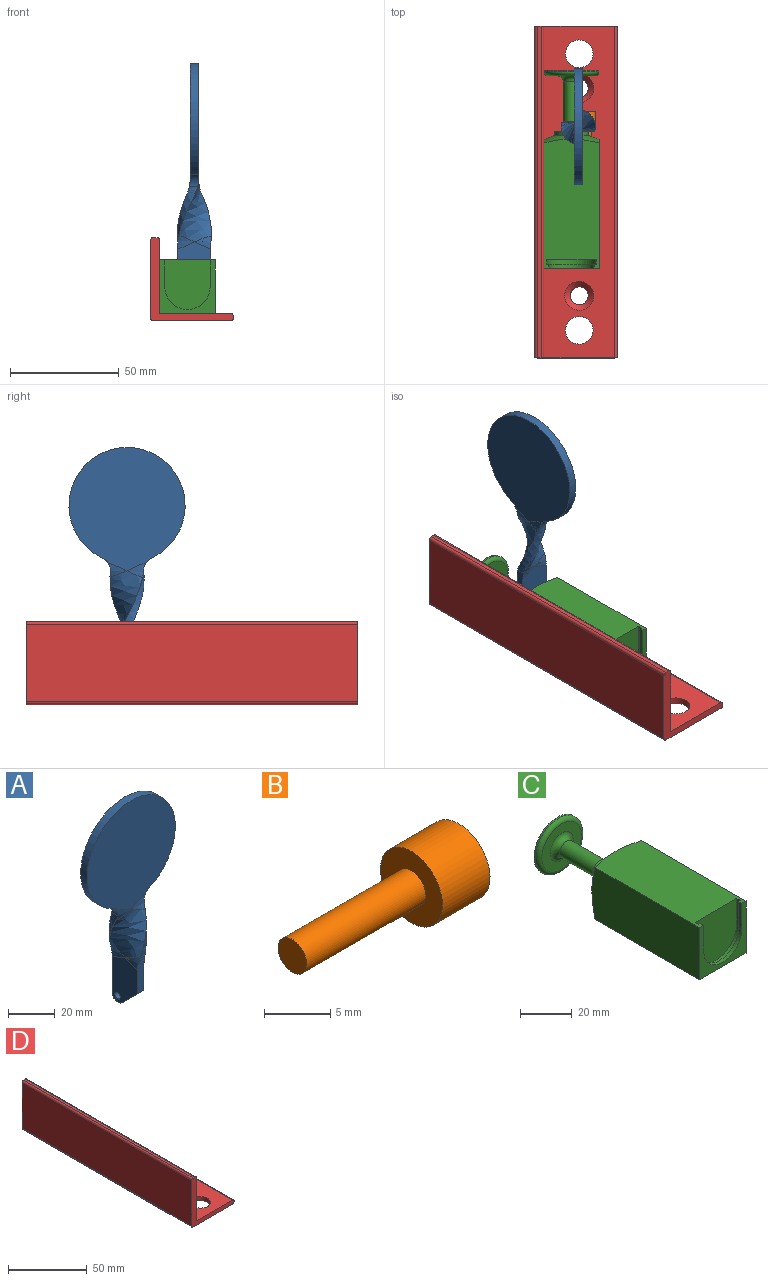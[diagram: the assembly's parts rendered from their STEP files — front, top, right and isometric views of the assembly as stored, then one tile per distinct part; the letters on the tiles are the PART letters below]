
ASSEMBLY  parts=4 mates=6
PART A: 26 faces, bbox 55x24.1x109.1 mm
  f0: plane 56.59x53.34mm, normal (0,-1,0), area 2267.7mm2, adj f2,f3,f4,f20,f21
  f1: plane 58.14x54.89mm, normal (0,1,0), area 2267.7mm2, adj f2,f3,f4,f18,f19
  f2: cylinder r=6.35mm len=5.75mm, axis (0,1,0), area 27.5mm2, adj f0,f1,f4,f5,f18,f20
  f3: cylinder r=6.35mm len=5.75mm, axis (0,1,0), area 27.5mm2, adj f0,f1,f4,f7,f19,f21
  f4: cylinder r=26.67mm len=53.34mm, axis (0,1,0), area 549.7mm2, adj f0,f1,f2,f3
  f5: bspline ~25.4x10.4mm, area 97.2mm2, adj f2,f6,f8,f9,f15,f16,f18,f20
  f6: bspline ~25.4x15.62mm, area 353.4mm2, adj f5,f7,f16,f17,f18,f19
  f7: bspline ~25.4x10.4mm, area 97.2mm2, adj f3,f6,f8,f11,f14,f17,f19,f21
  f8: bspline ~25.4x15.62mm, area 353.4mm2, adj f5,f7,f14,f15,f20,f21
  f9: plane 22.37x4.34mm, normal (0,1,0), area 84.7mm2, adj f5,f10,f12,f15,f16,f22
  f10: plane 27.09x16.93mm, normal (1,0,0), area 299mm2, adj f9,f11,f13,f16,f17,f22,f23,f24
  f11: plane 15.38x4.34mm, normal (0,-1,0), area 58.1mm2, adj f7,f10,f12,f14,f17,f23
  f12: plane 27.09x16.93mm, normal (-1,0,0), area 299mm2, adj f9,f11,f13,f14,f15,f22,f23,f24
  f13: plane 3.81x0.59mm, normal (0,0,-1), area 2.2mm2, adj f10,f12,f22,f24
  f14: bspline ~11.16x7.13mm, area 16.6mm2, adj f7,f8,f11,f12
  f15: bspline ~11.2x7.54mm, area 27.2mm2, adj f5,f8,f9,f12
  f16: bspline ~11.16x7.13mm, area 16.6mm2, adj f5,f6,f9,f10
  f17: bspline ~11.2x7.54mm, area 27.2mm2, adj f6,f7,f10,f11
  f18: bspline ~13.08x8.28mm, area 21.3mm2, adj f1,f2,f5,f6
  f19: bspline ~12.31x7.62mm, area 17.7mm2, adj f1,f3,f6,f7
  f20: bspline ~12.31x7.62mm, area 27.1mm2, adj f0,f2,f5,f8
  f21: bspline ~13.08x8.28mm, area 29.3mm2, adj f0,f3,f7,f8
  f22: cylinder r=3.17mm len=3.81mm, axis (-1,0,0), area 19mm2, adj f9,f10,f12,f13
  f23: plane 9.23x9.23mm, normal (0,-0.71,-0.71), area 49.7mm2, adj f10,f11,f12,f24
  f24: cylinder r=3.17mm len=3.81mm, axis (-1,0,0), area 9.5mm2, adj f10,f12,f13,f23
  f25: cylinder r=1.59mm len=3.81mm, axis (1,0,0), area 38mm2, adj f10,f12
PART B: 12 faces, bbox 17.8x6.6x6.6 mm
  f0: cylinder r=1.52mm len=12.7mm, axis (1,0,0), area 121.6mm2, adj f1,f4
  f1: plane 3.05x3.05mm, normal (-1,0,0), area 7.3mm2, adj f0
  f2: cylinder r=3.3mm len=6.6mm, axis (-1,0,0), area 105.4mm2, adj f3,f4
  f3: plane 6.6x6.6mm, normal (1,0,0), area 17.1mm2, adj f2,f5,f6,f7,f8,f9,f10
  f4: plane 6.6x6.6mm, normal (-1,0,0), area 27mm2, adj f0,f2
  f5: plane 3.05x2.22mm, normal (0,0.87,0.5), area 7.8mm2, adj f3,f6,f10,f11
  f6: plane 3.05x2.57mm, normal (0,0,1), area 7.8mm2, adj f3,f5,f7,f11
  f7: plane 3.05x2.22mm, normal (0,-0.87,0.5), area 7.8mm2, adj f3,f6,f8,f11
  f8: plane 3.05x2.22mm, normal (0,-0.87,-0.5), area 7.8mm2, adj f3,f7,f9,f11
  f9: plane 3.05x2.57mm, normal (0,0,-1), area 7.8mm2, adj f3,f8,f10,f11
  f10: plane 3.05x2.22mm, normal (0,0.87,-0.5), area 7.8mm2, adj f3,f5,f9,f11
  f11: plane 5.13x4.45mm, normal (1,0,0), area 17.1mm2, adj f5,f6,f7,f8,f9,f10
PART C: 31 faces, bbox 35.9x91.3x35.9 mm
  f0: plane 15.24x15.24mm, normal (0,1,0), area 156.7mm2, adj f9,f11,f12,f29
  f1: plane 59.31x25.41mm, normal (0,0,1), area 1405.7mm2, adj f2,f5,f6,f8,f10,f20,f21,f22
  f2: plane 25.4x24.69mm, normal (0,-1,0), area 199.6mm2, adj f1,f3,f6,f7,f8,f21,f22,f27
  f3: cylinder r=10.41mm len=20.82mm, axis (0,-1,0), area 56.9mm2, adj f2,f5,f27,f28
  f4: cylinder r=11.37mm len=22.72mm, axis (0,-1,0), area 71.1mm2, adj f5,f20,f25,f26
  f5: plane 23.71x22.73mm, normal (0,1,0), area 56.1mm2, adj f1,f3,f4,f21,f22,f23,f24,f25
  f6: plane 59.06x24.69mm, normal (-1,0,0), area 1442.4mm2, adj f1,f2,f7,f10
  f7: plane 59.06x25.41mm, normal (0,0,-1), area 1483.3mm2, adj f2,f6,f8,f10
  f8: plane 59.06x24.69mm, normal (1,0,0), area 1442.4mm2, adj f1,f2,f7,f10
  f9: cylinder r=7.62mm len=15.24mm, axis (0,1,0), area 91mm2, adj f0,f10,f29
  f10: cone r=7.62mm half-angle=70.7deg, axis (0,-1,0), area 465.8mm2, adj f1,f6,f7,f8,f9,f29
  f11: cylinder r=3.81mm len=22.86mm, axis (0,-1,0), area 492.5mm2, adj f0,f12,f14,f18
  f12: plane 7.62x4.57mm, normal (0,0,1), area 29.3mm2, adj f0,f11,f13,f14
  f13: plane 6.1x3.05mm, normal (0,-1,0), area 14.6mm2, adj f12,f14
  f14: torus R=3.05mm, axis (0,1,0), area 13.3mm2, adj f11,f12,f13
  f15: cylinder r=12.62mm len=25.25mm, axis (0,-1,0), area 60.4mm2, adj f16,f19
  f16: plane 25.25x25.25mm, normal (0,1,0), area 500.7mm2, adj f15
  f17: plane 21.69x21.69mm, normal (0,-1,0), area 242.9mm2, adj f18,f19
  f18: torus R=6.35mm, axis (0,1,0), area 118.7mm2, adj f11,f17
  f19: torus R=10.85mm, axis (0,1,0), area 210.2mm2, adj f15,f17
  f20: plane 23.71x22.73mm, normal (0,-1,0), area 483.5mm2, adj f1,f4,f23,f24,f25,f26
  f21: plane 12.7x1.78mm, normal (1,0,0), area 22.6mm2, adj f1,f2,f5,f28
  f22: plane 12.7x1.78mm, normal (-1,0,0), area 22.6mm2, adj f1,f2,f5,f27
  f23: plane 12.7x2.03mm, normal (-1,0,0), area 25.8mm2, adj f1,f5,f20,f26
  f24: plane 12.7x2.03mm, normal (1,0,0), area 25.8mm2, adj f1,f5,f20,f25
  f25: plane 2.03x0.01mm, normal (0,0,1), area 0mm2, adj f4,f5,f20,f24
  f26: plane 2.03x0.01mm, normal (0,0,1), area 0mm2, adj f4,f5,f20,f23
  f27: plane 1.78x0.01mm, normal (0,0,1), area 0mm2, adj f2,f3,f5,f22
  f28: plane 1.78x0.01mm, normal (0,0,1), area 0mm2, adj f2,f3,f5,f21
  f29: cylinder r=1.59mm len=12.7mm, axis (0,1,0), area 112.4mm2, adj f0,f9,f10,f30
  f30: plane 3.18x3.18mm, normal (0,1,0), area 7.9mm2, adj f29
PART D: 19 faces, bbox 38.1x152.4x38.1 mm
  f0: plane 152.4x32.58mm, normal (0,0,1), area 4431.8mm2, adj f2,f3,f11,f12,f14,f16,f17,f18
  f1: plane 152.4x35.56mm, normal (0,0,-1), area 5058.9mm2, adj f8,f9,f11,f12,f13,f14,f15,f16
  f2: cylinder r=1.27mm len=152.4mm, axis (0,1,0), area 304mm2, adj f0,f10,f11,f12
  f3: plane 152.4x33.66mm, normal (1,0,0), area 5129mm2, adj f0,f4,f11,f12
  f4: cylinder r=1.27mm len=152.4mm, axis (0,1,0), area 304mm2, adj f3,f5,f11,f12
  f5: plane 152.4x1.72mm, normal (0,0,1), area 261.3mm2, adj f4,f6,f11,f12
  f6: cylinder r=1.27mm len=152.4mm, axis (0,1,0), area 304mm2, adj f5,f7,f11,f12
  f7: plane 152.4x35.56mm, normal (-1,0,0), area 5419.3mm2, adj f6,f8,f11,f12
  f8: cylinder r=1.27mm len=152.4mm, axis (0,1,0), area 304mm2, adj f1,f7,f11,f12
  f9: cylinder r=1.27mm len=152.4mm, axis (0,1,0), area 304mm2, adj f1,f10,f11,f12
  f10: plane 152.4x0.64mm, normal (1,0,0), area 96.8mm2, adj f2,f9,f11,f12
  f11: plane 38.1x38.1mm, normal (0,-1,0), area 267.8mm2, adj f0,f1,f2,f3,f4,f5,f6,f7
  f12: plane 38.1x38.1mm, normal (0,1,0), area 267.8mm2, adj f0,f1,f2,f3,f4,f5,f6,f7
  f13: cylinder r=4.13mm len=8.26mm, axis (0,0,1), area 16.5mm2, adj f1,f18
  f14: cylinder r=6.35mm len=12.7mm, axis (0,0,1), area 126.7mm2, adj f0,f1
  f15: cylinder r=4.13mm len=8.26mm, axis (0,0,1), area 16.5mm2, adj f1,f17
  f16: cylinder r=6.35mm len=12.7mm, axis (0,0,1), area 126.7mm2, adj f0,f1
  f17: cone r=6.67mm half-angle=45deg, axis (0,0,1), area 121.8mm2, adj f0,f15
  f18: cone r=4.13mm half-angle=45deg, axis (0,0,1), area 121.8mm2, adj f0,f13
PLACE A rot(axis=(0,0,-1),90deg) t=(-29.29,20.86,77.3)mm
PLACE B rot(axis=(0,0,1),90deg) t=(-24.21,20.86,77.3)mm
PLACE C t=(-47.07,19.59,-10.91)mm
PLACE D t=(-47.07,16.42,-10.91)mm fixed
MATE cylindrical B.f0 <-> C.f29  axis (0,1,0) through (-26.75,16.41,-0.24)mm
MATE planar C.f7 <-> D.f0  axis (0,0,-1) through (-34.37,-14.71,-10.91)mm
MATE planar D.f3 <-> C.f6  axis (1,0,0) through (-47.07,-8.98,5.92)mm
MATE cylindrical B.f0 <-> A.f25  axis (0,-1,0) through (-26.75,22.76,-0.24)mm
MATE planar A.f12 <-> B.f0  axis (0,1,0) through (-30.65,22.76,10.22)mm
MATE planar A.f12 <-> C.f13  axis (0,1,0) through (-34.96,22.76,20.29)mm
